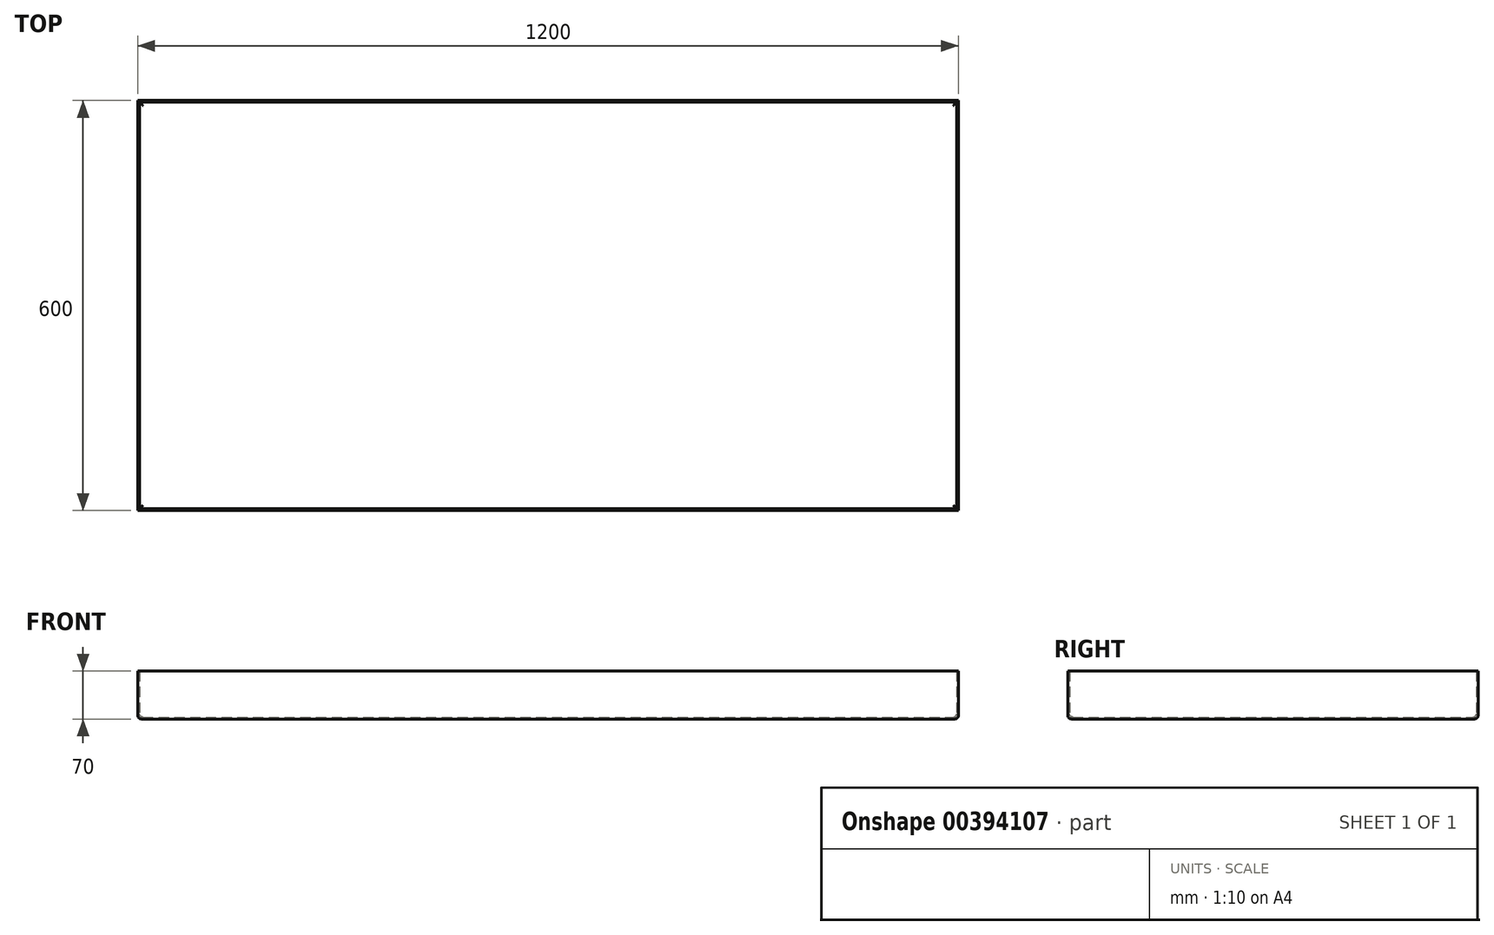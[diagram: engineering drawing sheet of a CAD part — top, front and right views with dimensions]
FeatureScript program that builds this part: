
annotation { "Feature Type Name" : "Feature", "Feature Type Description" : "" }
export const myFeature = defineFeature(function(context is Context, id is Id, definition is map)
    precondition{}
    {
        {
            var Q0;
            Q0=qCreatedBy(makeId("Top.planeOp"),FACE);
            var sketch = newSketch(context, id + "F0", { "sketchPlane" : qUnion([Q0])});
            skLineSegment(sketch, "E0.bottom", {"start": v(0, 0) * mm, "end": v(1200, 0) * mm});
            skLineSegment(sketch, "E0.top", {"start": v(0, 600) * mm, "end": v(1200, 600) * mm});
            skLineSegment(sketch, "E0.left", {"start": v(0, 0) * mm, "end": v(0, 600) * mm});
            skLineSegment(sketch, "E0.right", {"start": v(1200, 0) * mm, "end": v(1200, 600) * mm});
            skSolve(sketch);
        }
        {
            var Q0;
            Q0=makeQuery(id+"F0.imprint","IMPRINT",FACE,{"disambiguationData":[TD([[makeQuery(id+"F0.imprint","IMPRINT",EDGE,{"derivedFrom":sQuery(id+"F0.wireOp",EDGE,"E0.bottom")}),1.0]])]});
            extrude(context, id + "F1", {"entities" : qUnion([Q0]), "depth" : 70 * mm});
        }
        {
            var Q0;
            Q0=makeQuery(id+"F1.opExtrude","CAP_FACE",FACE,{"disambiguationData":[OSD([sQuery(id+"F0.wireOp",EDGE,"E0.bottom"),sQuery(id+"F0.wireOp",EDGE,"E0.top"),sQuery(id+"F0.wireOp",EDGE,"E0.left"),sQuery(id+"F0.wireOp",EDGE,"E0.right")])],"isStart":false});
            shell(context, id + "F2", {"entities" : qUnion([Q0]), "thickness" : 2.5 * mm});
        }
        {
            var Q0;
            Q0=makeQuery(id+"F1.opExtrude","CAP_FACE",FACE,{"disambiguationData":[OSD([sQuery(id+"F0.wireOp",EDGE,"E0.bottom"),sQuery(id+"F0.wireOp",EDGE,"E0.top"),sQuery(id+"F0.wireOp",EDGE,"E0.left"),sQuery(id+"F0.wireOp",EDGE,"E0.right")])],"isStart":true});
            fillet(context, id + "F3", {"entities" : qUnion([Q0]), "radius" : 5 * mm, "tangentPropagation" : true, "allowEdgeOverflow" : false});
        }
        {
            var Q0;
            Q0=makeQuery(id+"F2.opShell","OFFSET_FACE",FACE,{"disambiguationData":[OSD([sQuery(id+"F0.wireOp",EDGE,"E0.bottom"),sQuery(id+"F0.wireOp",EDGE,"E0.top"),sQuery(id+"F0.wireOp",EDGE,"E0.left"),sQuery(id+"F0.wireOp",EDGE,"E0.right")])]});
            fillet(context, id + "F4", {"entities" : qUnion([Q0]), "radius" : 5 * mm, "tangentPropagation" : true, "allowEdgeOverflow" : false});
        }
    });
